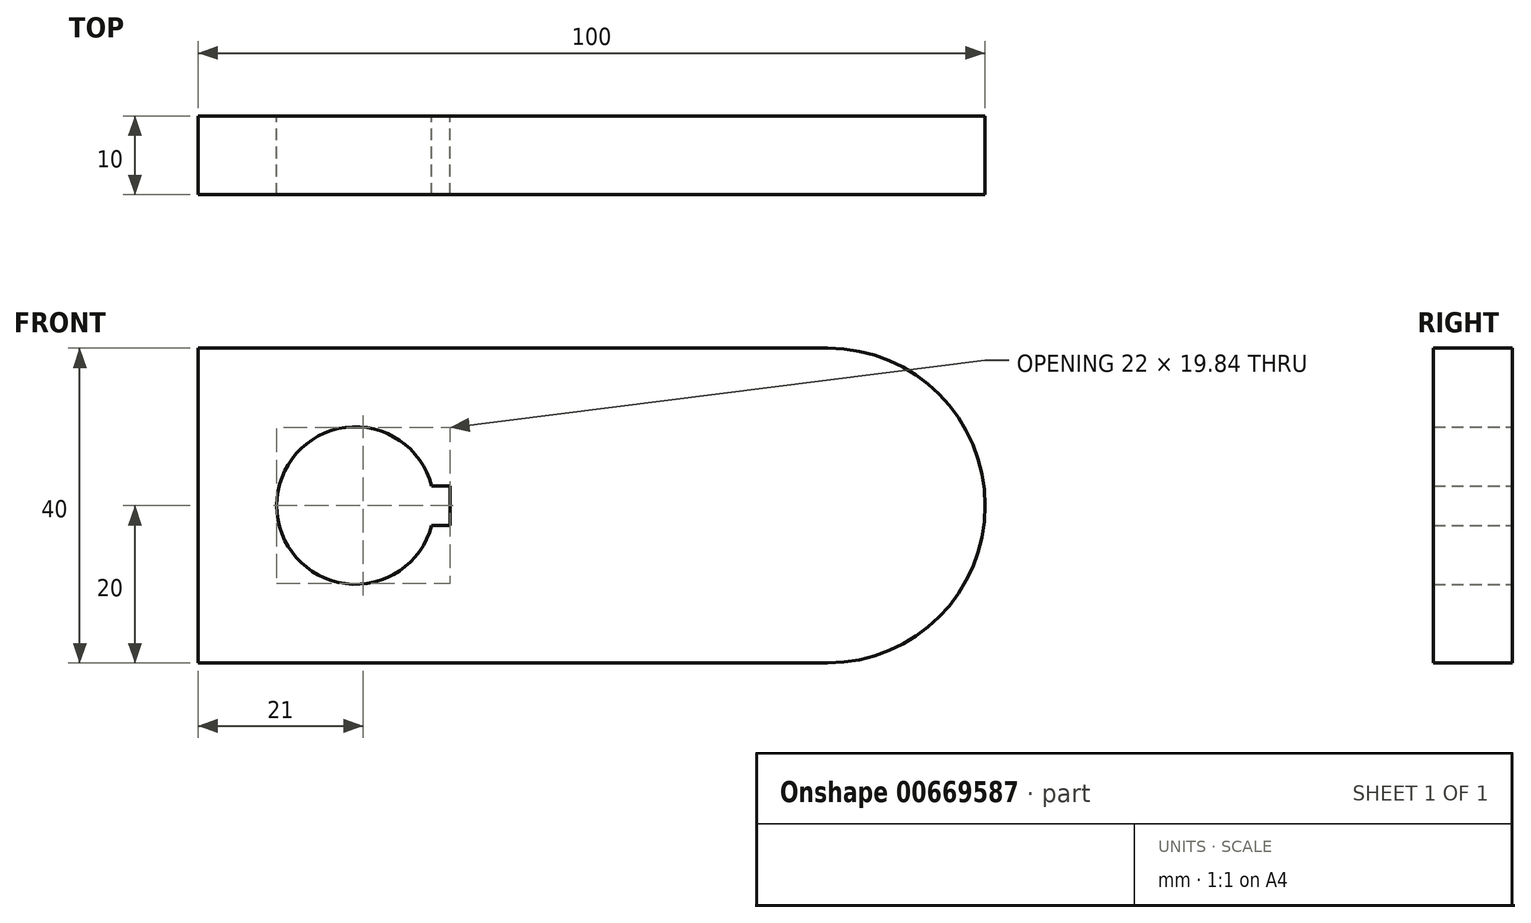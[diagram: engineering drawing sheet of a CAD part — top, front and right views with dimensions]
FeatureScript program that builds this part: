
annotation { "Feature Type Name" : "Feature", "Feature Type Description" : "" }
export const myFeature = defineFeature(function(context is Context, id is Id, definition is map)
    precondition{}
    {
        {
            var Q0;
            Q0=qCreatedBy(makeId("Front.planeOp"),FACE);
            var sketch = newSketch(context, id + "F0", { "sketchPlane" : qUnion([Q0])});
            skLineSegment(sketch, "E0.bottom", {"start": v(0, 40) * mm, "end": v(80, 40) * mm});
            skLineSegment(sketch, "E0.top", {"start": v(0, 0) * mm, "end": v(80, 0) * mm});
            skLineSegment(sketch, "E0.left", {"start": v(0, 40) * mm, "end": v(0, 0) * mm});
            skArc(sketch, "E1", {"start": v(29.68, 22.5) * mm, "mid": v(10, 20) * mm, "end": v(29.68, 17.5) * mm});
            skPoint(sketch, "E1.centerSnap0", {"position": v(0, 20) * mm});
            skArc(sketch, "E2", {"start": v(80, 0) * mm, "mid": v(100, 20) * mm, "end": v(80, 40) * mm});
            skPoint(sketch, "E3.orphan", {"position": v(100, 0) * mm});
            skLineSegment(sketch, "E4.bottom", {"start": v(32, 17.5) * mm, "end": v(29.68, 17.5) * mm});
            skLineSegment(sketch, "E4.top", {"start": v(32, 22.5) * mm, "end": v(29.68, 22.5) * mm});
            skLineSegment(sketch, "E4.left", {"start": v(32, 17.5) * mm, "end": v(32, 22.5) * mm});
            skPoint(sketch, "E4.middle", {"position": v(30, 20) * mm});
            skPoint(sketch, "E5.orphan", {"position": v(28, 22.5) * mm});
            skPoint(sketch, "E6.orphan", {"position": v(28, 17.5) * mm});
            skSolve(sketch);
        }
        {
            var Q0;
            Q0=makeQuery(id+"F0.imprint","IMPRINT",FACE,{"disambiguationData":[TD([[makeQuery(id+"F0.imprint","IMPRINT",EDGE,{"derivedFrom":sQuery(id+"F0.wireOp",EDGE,"E0.bottom")}),-1.0]])]});
            extrude(context, id + "F1", {"entities" : qUnion([Q0]), "depth" : 10 * mm, "offsetDistance" : 25 * mm});
        }
    });
